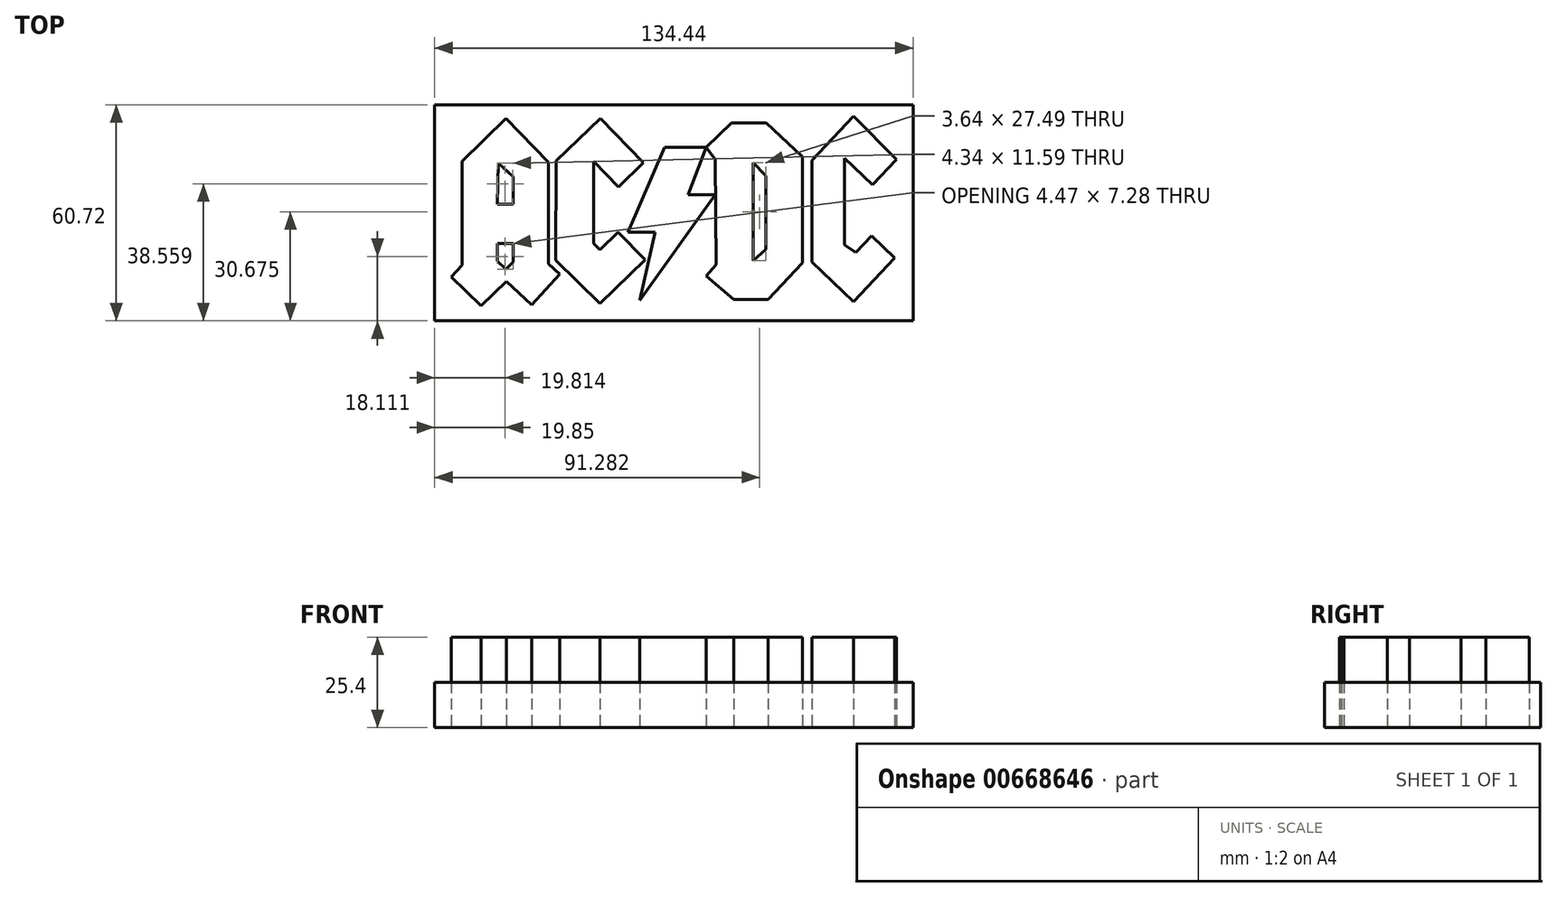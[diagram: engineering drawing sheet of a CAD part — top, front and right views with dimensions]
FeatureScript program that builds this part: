
annotation { "Feature Type Name" : "Feature", "Feature Type Description" : "" }
export const myFeature = defineFeature(function(context is Context, id is Id, definition is map)
    precondition{}
    {
        {
            var Q0;
            Q0=qCreatedBy(makeId("Top.planeOp"),FACE);
            var sketch = newSketch(context, id + "F0", { "sketchPlane" : qUnion([Q0])});
            skLineSegment(sketch, "E0", {"start": v(-58.95, 13) * mm, "end": v(-46.57, 25) * mm});
            skLineSegment(sketch, "E1", {"start": v(-46.57, 25) * mm, "end": v(-34.63, 12.68) * mm});
            skLineSegment(sketch, "E2", {"start": v(-34.63, 12.68) * mm, "end": v(-34.63, -15.84) * mm});
            skLineSegment(sketch, "E3", {"start": v(-34.63, -15.84) * mm, "end": v(-31.46, -18.76) * mm});
            skLineSegment(sketch, "E4", {"start": v(-31.46, -18.76) * mm, "end": v(-39.38, -27.38) * mm});
            skLineSegment(sketch, "E5", {"start": v(-39.38, -27.38) * mm, "end": v(-46.45, -20.89) * mm});
            skLineSegment(sketch, "E6", {"start": v(-46.45, -20.89) * mm, "end": v(-53.64, -27.69) * mm});
            skLineSegment(sketch, "E7", {"start": v(-53.64, -27.69) * mm, "end": v(-62.03, -19.53) * mm});
            skLineSegment(sketch, "E8", {"start": v(-62.03, -19.53) * mm, "end": v(-58.88, -16.3) * mm});
            skLineSegment(sketch, "E9", {"start": v(-58.88, -16.3) * mm, "end": v(-58.95, 13) * mm});
            skLineSegment(sketch, "E10", {"start": v(-49, 0.86) * mm, "end": v(-44.65, 0.86) * mm});
            skLineSegment(sketch, "E11", {"start": v(-44.65, 0.86) * mm, "end": v(-44.65, 8.68) * mm});
            skLineSegment(sketch, "E12", {"start": v(-44.65, 8.68) * mm, "end": v(-48.84, 12.46) * mm});
            skLineSegment(sketch, "E13", {"start": v(-48.84, 12.46) * mm, "end": v(-49, 0.86) * mm});
            skLineSegment(sketch, "E14", {"start": v(-32.47, 13.06) * mm, "end": v(-20.07, 25.08) * mm});
            skLineSegment(sketch, "E15", {"start": v(-20.07, 25.08) * mm, "end": v(-7.98, 12.61) * mm});
            skLineSegment(sketch, "E16", {"start": v(-7.98, 12.61) * mm, "end": v(-15.05, 5.76) * mm});
            skLineSegment(sketch, "E17", {"start": v(-15.05, 5.76) * mm, "end": v(-22.02, 12.94) * mm});
            skLineSegment(sketch, "E18", {"start": v(-22.02, 12.94) * mm, "end": v(-22.02, -10.15) * mm});
            skLineSegment(sketch, "E19", {"start": v(-22.02, -10.15) * mm, "end": v(-20.26, -11.97) * mm});
            skLineSegment(sketch, "E20", {"start": v(-20.26, -11.97) * mm, "end": v(-15.1, -6.96) * mm});
            skLineSegment(sketch, "E21", {"start": v(-15.1, -6.96) * mm, "end": v(-7.52, -14.78) * mm});
            skLineSegment(sketch, "E22", {"start": v(-7.52, -14.78) * mm, "end": v(-20.17, -27.04) * mm});
            skLineSegment(sketch, "E23", {"start": v(-20.17, -27.04) * mm, "end": v(-32.6, -14.83) * mm});
            skLineSegment(sketch, "E24", {"start": v(-32.6, -14.83) * mm, "end": v(-32.47, 13.06) * mm});
            skLineSegment(sketch, "E25", {"start": v(-2.02, 16.9) * mm, "end": v(9.7, 16.9) * mm});
            skLineSegment(sketch, "E26", {"start": v(9.7, 16.9) * mm, "end": v(4.53, 3.6) * mm});
            skLineSegment(sketch, "E27", {"start": v(4.53, 3.6) * mm, "end": v(12.17, 3.6) * mm});
            skLineSegment(sketch, "E28", {"start": v(12.17, 3.6) * mm, "end": v(-9, -26.2) * mm});
            skLineSegment(sketch, "E29", {"start": v(-9, -26.2) * mm, "end": v(-4.7, -7.04) * mm});
            skLineSegment(sketch, "E30", {"start": v(-4.7, -7.04) * mm, "end": v(-12.28, -7.04) * mm});
            skLineSegment(sketch, "E31", {"start": v(-12.28, -7.04) * mm, "end": v(-2.02, 16.9) * mm});
            skLineSegment(sketch, "E32", {"start": v(9.7, 16.9) * mm, "end": v(16.72, 23.78) * mm});
            skLineSegment(sketch, "E33", {"start": v(16.72, 23.78) * mm, "end": v(26.54, 23.78) * mm});
            skLineSegment(sketch, "E34", {"start": v(26.54, 23.78) * mm, "end": v(36.7, 14.18) * mm});
            skLineSegment(sketch, "E35", {"start": v(36.7, 14.18) * mm, "end": v(36.7, -15.63) * mm});
            skLineSegment(sketch, "E36", {"start": v(36.7, -15.63) * mm, "end": v(26.99, -25.9) * mm});
            skLineSegment(sketch, "E37", {"start": v(26.99, -25.9) * mm, "end": v(17.38, -25.9) * mm});
            skLineSegment(sketch, "E38", {"start": v(17.38, -25.9) * mm, "end": v(9.7, -19.28) * mm});
            skLineSegment(sketch, "E39", {"start": v(9.7, -19.28) * mm, "end": v(12.45, -16.08) * mm});
            skLineSegment(sketch, "E40", {"start": v(12.45, -16.08) * mm, "end": v(12.17, 13.4) * mm});
            skLineSegment(sketch, "E41", {"start": v(12.17, 13.4) * mm, "end": v(9.7, 16.9) * mm});
            skLineSegment(sketch, "E42", {"start": v(22.9, 12.52) * mm, "end": v(26.43, 8.88) * mm});
            skLineSegment(sketch, "E43", {"start": v(26.43, 8.88) * mm, "end": v(26.43, -11.77) * mm});
            skLineSegment(sketch, "E44", {"start": v(26.43, -11.77) * mm, "end": v(22.8, -14.97) * mm});
            skLineSegment(sketch, "E45", {"start": v(22.8, -14.97) * mm, "end": v(22.9, 12.52) * mm});
            skLineSegment(sketch, "E46", {"start": v(51.06, 25.66) * mm, "end": v(39.3, 13.23) * mm});
            skLineSegment(sketch, "E47", {"start": v(39.3, 13.23) * mm, "end": v(39.3, -15.41) * mm});
            skLineSegment(sketch, "E48", {"start": v(39.3, -15.41) * mm, "end": v(51, -26.49) * mm});
            skLineSegment(sketch, "E49", {"start": v(51, -26.49) * mm, "end": v(62.62, -14.21) * mm});
            skLineSegment(sketch, "E50", {"start": v(62.62, -14.21) * mm, "end": v(56.12, -8.06) * mm});
            skLineSegment(sketch, "E51", {"start": v(56.12, -8.06) * mm, "end": v(51.68, -12.75) * mm});
            skLineSegment(sketch, "E52", {"start": v(51.68, -12.75) * mm, "end": v(48.55, -10.54) * mm});
            skLineSegment(sketch, "E53", {"start": v(48.55, -10.54) * mm, "end": v(48.55, 13.87) * mm});
            skLineSegment(sketch, "E54", {"start": v(48.55, 13.87) * mm, "end": v(56.44, 6.4) * mm});
            skLineSegment(sketch, "E55", {"start": v(56.44, 6.4) * mm, "end": v(63.07, 13.41) * mm});
            skLineSegment(sketch, "E56", {"start": v(63.07, 13.41) * mm, "end": v(51.06, 25.66) * mm});
            skLineSegment(sketch, "E57", {"start": v(-49.09, -15.07) * mm, "end": v(-46.6, -17.43) * mm});
            skLineSegment(sketch, "E58", {"start": v(-46.6, -17.43) * mm, "end": v(-44.62, -15.34) * mm});
            skLineSegment(sketch, "E59", {"start": v(-44.62, -15.34) * mm, "end": v(-44.64, -10.15) * mm});
            skLineSegment(sketch, "E60", {"start": v(-44.64, -10.15) * mm, "end": v(-49.09, -10.16) * mm});
            skLineSegment(sketch, "E61", {"start": v(-49.09, -10.16) * mm, "end": v(-49.09, -15.07) * mm});
            skSolve(sketch);
        }
        {
            var Q0;
            Q0=qCreatedBy(makeId("Top.planeOp"),FACE);
            var sketch = newSketch(context, id + "F1", { "sketchPlane" : qUnion([Q0])});
            skLineSegment(sketch, "E62.bottom", {"start": v(-66.67, 28.82) * mm, "end": v(67.77, 28.82) * mm});
            skLineSegment(sketch, "E62.top", {"start": v(-66.67, -31.9) * mm, "end": v(67.77, -31.9) * mm});
            skLineSegment(sketch, "E62.left", {"start": v(-66.67, 28.82) * mm, "end": v(-66.67, -31.9) * mm});
            skLineSegment(sketch, "E62.right", {"start": v(67.77, 28.82) * mm, "end": v(67.77, -31.9) * mm});
            skSolve(sketch);
        }
        {
            var Q0;
            Q0 = qSketchRegion(id + "F0", true);
            extrude(context, id + "F2", {"entities" : qUnion([Q0]), "depth" : 25.4 * mm, "offsetDistance" : 25.4 * mm});
        }
        {
            var Q0;
            Q0 = qSketchRegion(id + "F1", true);
            extrude(context, id + "F3", {"entities" : qUnion([Q0]), "depth" : 12.7 * mm, "offsetDistance" : 25.4 * mm});
        }
    });
